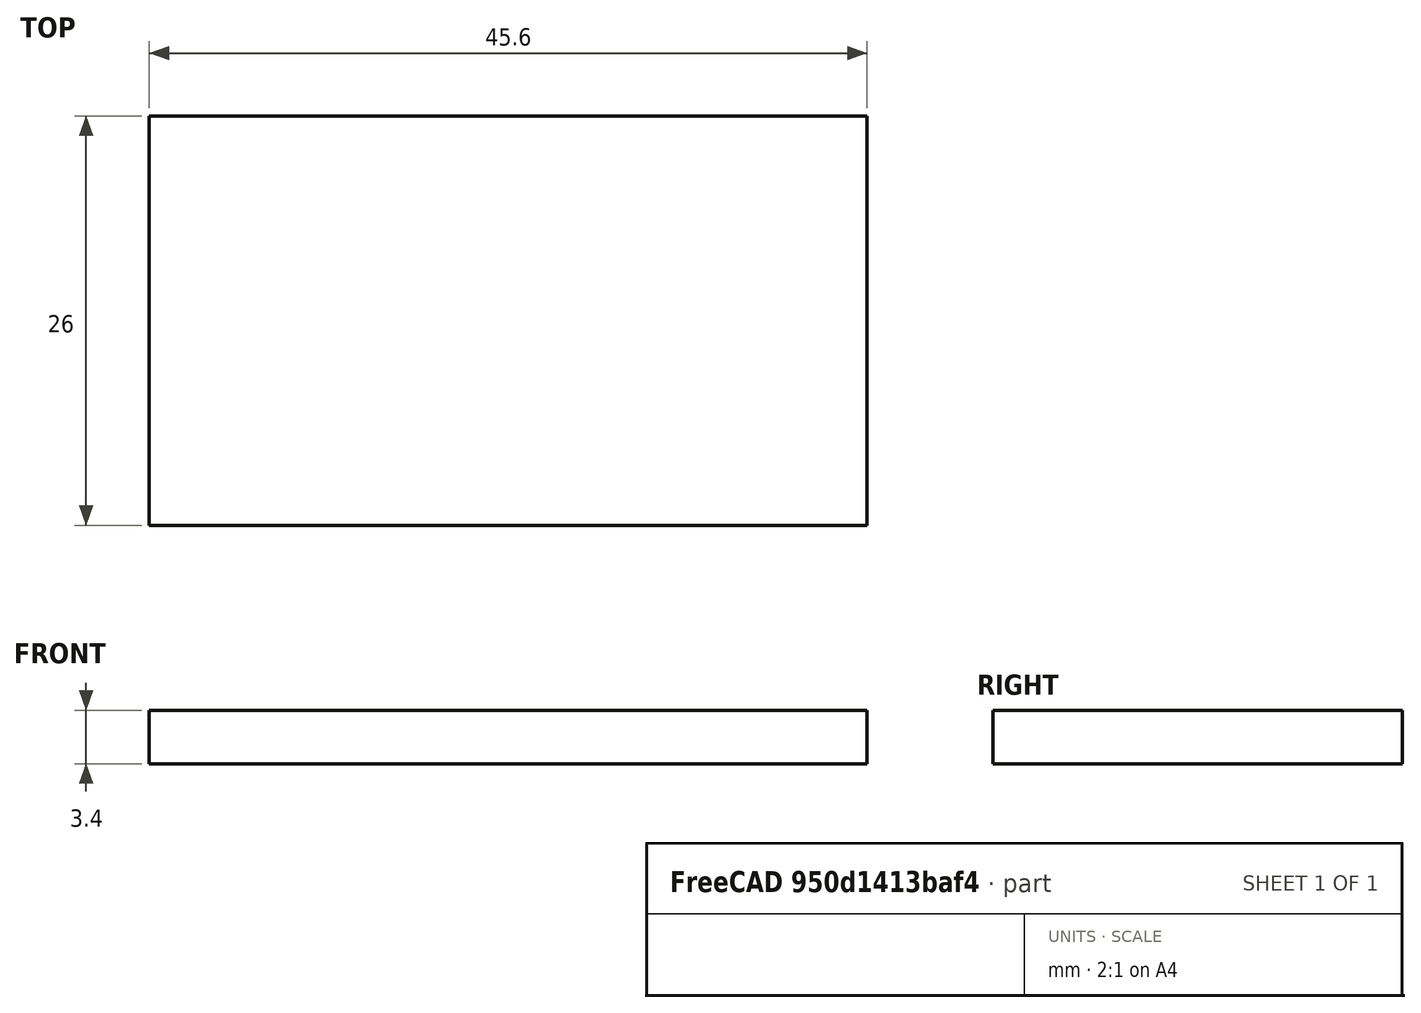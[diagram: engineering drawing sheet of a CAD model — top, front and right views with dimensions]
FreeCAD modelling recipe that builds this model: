
FCSTD DOCUMENT  (FreeCAD 0.17R12703 (Git))
Label: Servotraeger_unten
License: All rights reserved
LicenseURL: http://en.wikipedia.org/wiki/All_rights_reserved
objects: Path::FeaturePython×7, Part::FeaturePython×2, Part::Feature×1, App::FeaturePython×1, Path::FeatureCompoundPython×1
note: 5 computed .brp shape members not serialized (recipe doc carries the construction recipe); baked Part::Feature solids carry a one-line shape summary decoded from their .brp

FEATURE [Part::Feature] Part__Feature  label="Servotraeger_unten"
  Placement = pos=(0,0,-3.4) rot=(0,0,1;0rad)
  shape: bbox 45.6 x 26 x 3.4 mm, 20 faces (baked)
FEATURE [App::FeaturePython] SetupSheet  # Path/CAM operation (typed FeaturePython)
  ClearanceHeightExpression = StartDepth+SetupSheet.ClearanceHeightOffset
  ClearanceHeightOffset = 5
  FinalDepthExpression = OpFinalDepth
  HorizRapid = 0
  SafeHeightExpression = StartDepth+SetupSheet.SafeHeightOffset
  SafeHeightOffset = 3
  StartDepthExpression = OpStartDepth
  StepDownExpression = OpToolDiameter
  VertRapid = 0
FEATURE [Part::FeaturePython] Clone  label="Base-Servotraeger_unten"  # Draft clone (typed FeaturePython)
  AttacherType = Attacher::AttachEngine3D
  Fuse = false
  Objects = -> [Part__Feature]
  PathResource = Base
  Placement = pos=(0,0,-3.4) rot=(0,0,1;0rad)
  Scale = (1,1,1)
FEATURE [Part::FeaturePython] Stock  # WARN: FeaturePython — macro-defined, semantics opaque (R4)
  Base = -> Part__Feature
  ExtXneg = 0
  ExtXpos = 0
  ExtYneg = 0
  ExtYpos = 0
  ExtZneg = 0
  ExtZpos = 0
  StockType = FromBase
FEATURE [Path::FeaturePython] T1__Schaftfraeser_D2  label="T1: Schaftfraeser_D2"  # Path/CAM operation (typed FeaturePython)
  HorizFeed = 400
  HorizRapid = 0
  SpindleDir = 0
  SpindleSpeed = 0
  ToolNumber = 1
  VertFeed = 100
  VertRapid = 0
  expr: HorizRapid = SetupSheet.HorizRapid
  expr: VertRapid = SetupSheet.VertRapid
FEATURE [Path::FeaturePython] Profile_Faces  # Path/CAM operation (typed FeaturePython)
  Active = true
  AreaParams:
    OpenMode = 0
    Angle = 45.0
    MinArcPoints = 4
    Coplanar = 0
    Tolerance = 1e-07
    CleanDistance = 0.0
    PocketExtraOffset = 0.0
    AngleShift = 0.0
    SubjectFill = 0
    RoundPreceision = 0.0
    Simplify = False
    SectionTolerance = 1e-06
    MaxArcPoints = 100
    SectionOffset = 0.0
    Offset = -1.0
    Accuracy = 0.01
    PocketStepover = 0.0
    ClipFill = 0
    ToolRadius = 1.0
    Outline = False
    ClipperScale = 10000000.0
    FromCenter = False
    Explode = False
    EndType = 0
    Shift = 0.0
    ExtraPass = 0
    Project = False
    JoinType = 0
    Thicken = False
    Stepdown = 1.0
    SectionMode = 2
    MiterLimit = 2.0
    Deflection = 0.01
    Reorient = True
    FitArcs = True
    SectionCount = -1
    PocketMode = 0
    Stepover = 0.0
    Unit = 1.0
    Fill = 0
  Base = -> [Clone]
  ClearanceHeight = 5
  Direction = 0
  FinalDepth = -3.7
  JoinType = 0
  MiterLimit = 0.1
  OffsetExtra = 0
  OpFinalDepth = -3.4
  OpStartDepth = 0
  OpToolDiameter = 2
  PathParams = {'resume_height': 3.0, 'feedrate': 400.0, 'verbose': True, 'orientation': 1, 'return_end': True, 'preamble': False, 'retraction': 5.0, 'feedrate_v': 100.0}
  SafeHeight = 3
  Side = 1
  StartDepth = 0
  StartPoint = (0,0,0)
  StepDown = 2
  ToolController = -> T1__Schaftfraeser_D2
  UseComp = true
  UseStartPoint = false
  processCircles = false
  processHoles = false
  processPerimeter = true
  expr: ClearanceHeight = StartDepth + SetupSheet.ClearanceHeightOffset
  expr: SafeHeight = StartDepth + SetupSheet.SafeHeightOffset
  expr: StepDown = 2
  expr: FinalDepth = -3.7000000000000002
  expr: StartDepth = OpStartDepth
FEATURE [Path::FeaturePython] DogboneDressup  # Path/CAM operation (typed FeaturePython)
  Base = -> Profile_Faces
  Custom = 0
  Incision = 0
  Side = 0
  Style = 0
  ToolController = -> T1__Schaftfraeser_D2
FEATURE [Path::FeaturePython] Contour  # Path/CAM operation (typed FeaturePython)
  Active = true
  AreaParams:
    OpenMode = 0
    Angle = 45.0
    MinArcPoints = 4
    Coplanar = 2
    Tolerance = 1e-07
    CleanDistance = 0.0
    PocketExtraOffset = 0.0
    AngleShift = 0.0
    SubjectFill = 0
    RoundPreceision = 0.0
    Simplify = False
    SectionTolerance = 1e-06
    MaxArcPoints = 100
    SectionOffset = 0.0
    Offset = 1.0
    Accuracy = 0.01
    PocketStepover = 0.0
    ClipFill = 0
    ToolRadius = 1.0
    Outline = False
    ClipperScale = 10000000.0
    FromCenter = False
    Explode = False
    EndType = 0
    Shift = 0.0
    ExtraPass = 0
    Project = False
    JoinType = 0
    Thicken = False
    Stepdown = 1.0
    SectionMode = 2
    MiterLimit = 2.0
    Deflection = 0.01
    Reorient = True
    FitArcs = True
    SectionCount = -1
    PocketMode = 0
    Stepover = 0.0
    Unit = 1.0
    Fill = 0
  ClearanceHeight = 5
  Direction = 1
  FinalDepth = -3.7
  JoinType = 0
  MiterLimit = 0.1
  OffsetExtra = 0
  OpFinalDepth = -3.4
  OpStartDepth = 0
  OpToolDiameter = 2
  PathParams = {'resume_height': 3.0, 'feedrate': 400.0, 'verbose': True, 'orientation': 0, 'return_end': True, 'preamble': False, 'retraction': 5.0, 'feedrate_v': 100.0}
  SafeHeight = 3
  Side = 0
  StartDepth = 0
  StartPoint = (0,0,0)
  StepDown = 2
  ToolController = -> T1__Schaftfraeser_D2
  UseComp = true
  UseStartPoint = false
  expr: ClearanceHeight = StartDepth + SetupSheet.ClearanceHeightOffset
  expr: SafeHeight = StartDepth + SetupSheet.SafeHeightOffset
  expr: StepDown = 2
  expr: FinalDepth = -3.7000000000000002
  expr: StartDepth = OpStartDepth
FEATURE [Path::FeaturePython] DogboneDressup001  # Path/CAM operation (typed FeaturePython)
  Base = -> Contour
  Custom = 0
  Incision = 0
  Side = 0
  Style = 0
  ToolController = -> T1__Schaftfraeser_D2
FEATURE [Path::FeaturePython] TagDressup  # Path/CAM operation (typed FeaturePython)
  Angle = 45
  Base = -> DogboneDressup001
  Height = 1.6
  Positions = (3) [(30.9003,27,0),(-1,13.4966,0),(42.0116,-1,0)]
  Radius = 0
  SegmentationFactor = 50
  Width = 4
FEATURE [Path::FeatureCompoundPython] Operations  # Path/CAM operation (typed FeaturePython)
  Group = -> [DogboneDressup,TagDressup]
  UsePlacements = false
FEATURE [Path::FeaturePython] Job  # Path/CAM operation (typed FeaturePython)
  Base = -> Clone
  GeometryTolerance = 0.01
  Operations = -> Operations
  PostProcessor = 5
  SetupSheet = -> SetupSheet
  Stock = -> Stock
  ToolController = -> [T1__Schaftfraeser_D2]
